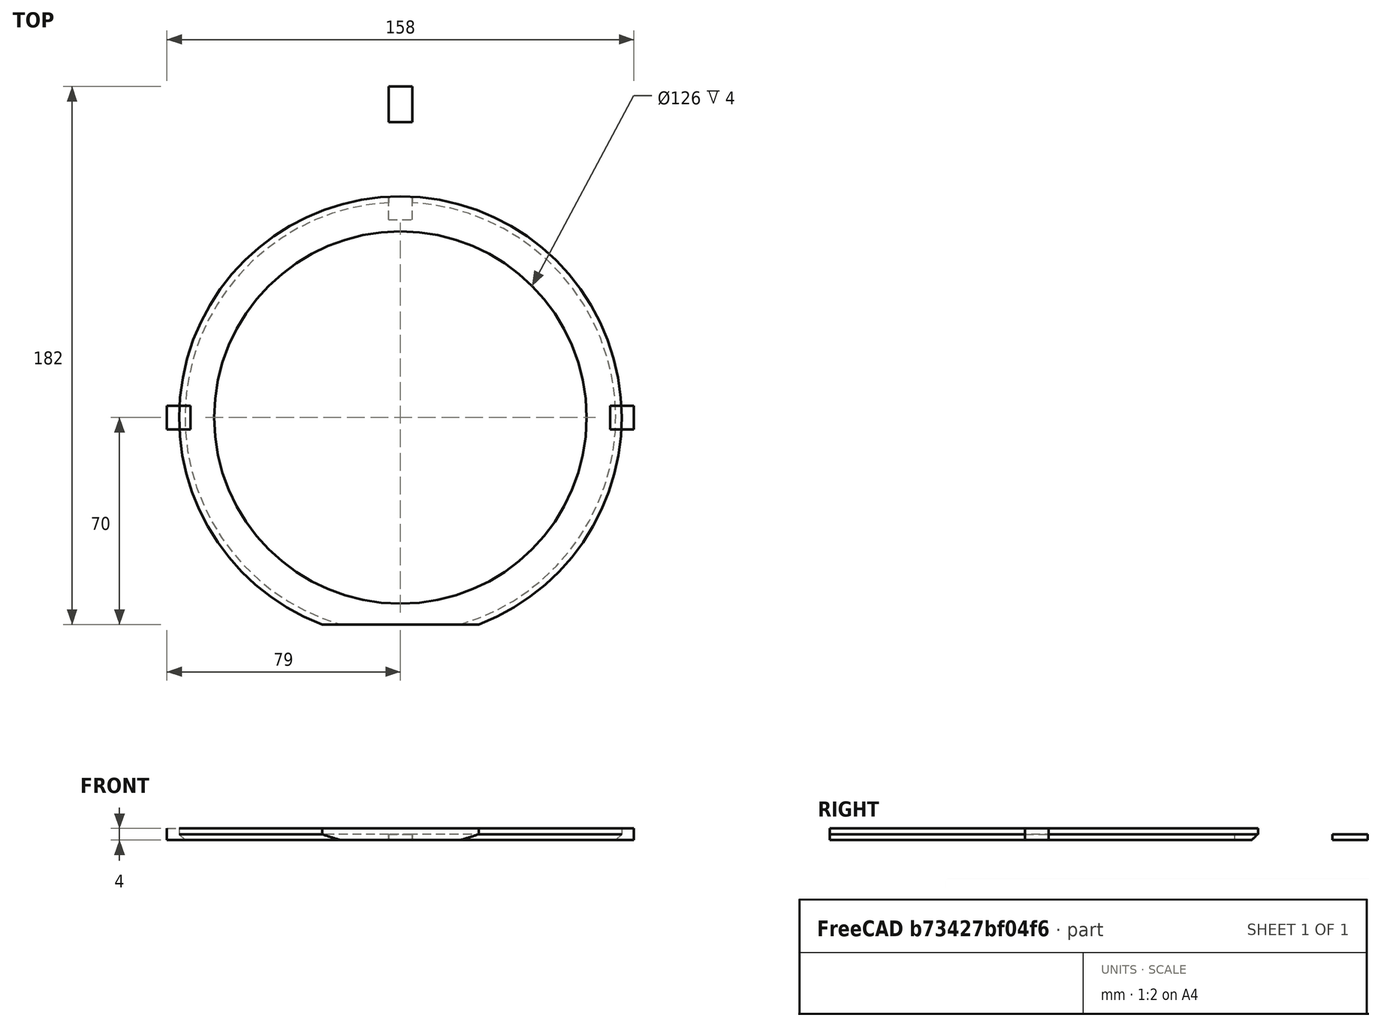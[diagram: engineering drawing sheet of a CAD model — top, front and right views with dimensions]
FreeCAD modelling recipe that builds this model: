
FCSTD DOCUMENT  (FreeCAD 0.19R0.19.2)
Label: waferHolder_004
License: All rights reserved
LicenseURL: http://en.wikipedia.org/wiki/All_rights_reserved
objects: Part::Box×4, Sketcher::SketchObject×1, Part::Extrusion×1, Part::Chamfer×1, Part::Cut×1
note: 8 computed .brp shape members not serialized (recipe doc carries the construction recipe); baked Part::Feature solids carry a one-line shape summary decoded from their .brp

FEATURE [Sketcher::SketchObject] Sketch
  FullyConstrained = true
  sketch-geometry (3):
    g0: Circle CenterX=-3.1415e-12 CenterY=5.6243e-12 CenterZ=0 NormalX=0 NormalY=0 NormalZ=1 AngleXU=0 Radius=63
    g1: ArcOfCircle CenterX=-3.1415e-12 CenterY=5.6243e-12 CenterZ=0 NormalX=0 NormalY=0 NormalZ=1 AngleXU=0 Radius=74.8482 StartAngle=5.07429 EndAngle=10.6337
    g2: LineSegment StartX=-26.5 StartY=-70.0001 StartZ=0 EndX=26.5 EndY=-70.0001 EndZ=0
  constraints (6):
    c: Block(g0)
    c: Coincident(g1,g0)
    c: Block(g1)
    c: Coincident(g2,g1)
    c: Coincident(g2,g1)
    c: Horizontal(g2)
FEATURE [Part::Box] Box  label="holderBitLeft"
  AttacherType = Attacher::AttachEngine3D
  Height = 4
  Length = 8
  Placement = pos=(-79,-4,0) rot=(0,0,1;0rad)
  Width = 8
FEATURE [Part::Box] Box001  label="bitHolderTopCutout"
  AttacherType = Attacher::AttachEngine3D
  Height = 4
  Length = 8
  Placement = pos=(-4,67,-2) rot=(0,0,1;0rad)
  Width = 12
FEATURE [Part::Extrusion] Extrude  label="mainHolderRing"
  Base = -> Sketch
  Dir = (0,0,1)
  DirMode = 2
  FaceMakerClass = Part::FaceMakerBullseye
  LengthFwd = 4
  LengthRev = 0
  Solid = true
  Symmetric = false
FEATURE [Part::Box] Box002  label="holderBitRight"
  AttacherType = Attacher::AttachEngine3D
  Height = 4
  Length = 8
  Placement = pos=(71,-4,0) rot=(0,0,1;0rad)
  Width = 8
FEATURE [Part::Box] Box003  label="bitHolderTop"
  AttacherType = Attacher::AttachEngine3D
  Height = 2
  Length = 8
  Placement = pos=(-4,100,0) rot=(0,0,1;0rad)
  Width = 12
FEATURE [Part::Chamfer] Chamfer
  Base = -> Extrude
  Edges = 1 edges r=2: [Edge3]
FEATURE [Part::Cut] Cut
  Base = -> Chamfer
  Tool = -> Box001
